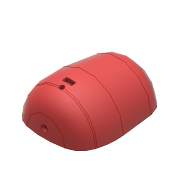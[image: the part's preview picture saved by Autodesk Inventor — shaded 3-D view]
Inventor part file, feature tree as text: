
AUTODESK INVENTOR PART (.ipt)
format: ipt  version: 2017 (Build 210142000, 142)  size: 274,944 bytes
history: native  units: mm
features: sketch x9, extrude x7, fillet x4, projected_geometry x2, revolve x1, chamfer x1, shell x1, hole x1, plane x1
ambient origin geometry x8: Origin, YZ Plane, XZ Plane, XY Plane, X Axis, Y Axis, Z Axis, Center Point
bodies: Solid1 (feature_tree)
feature tree (27):
  revolve  "Revolution1"  [1 undecoded]
  fillet  "Fillet1"  Radius=30.0mm
  chamfer  "Chamfer1"  Distance=10.0mm Angle=45.0deg
  fillet  "Fillet2"  Radius=20.0mm
  fillet  "Fillet3"  Radius=60.0mm
  extrude  "Extrusion1"  Depth=10.0mm
  shell  "Shell1"  Thickness=100.0mm
  extrude  "Extrusion3"  Depth=12.0mm
  extrude  "Extrusion4"  Depth=8.0mm
  hole  "Hole1"  [1 undecoded]
  plane  "Work Plane1"
  extrude  "Extrusion5"  [1 undecoded]
  fillet  "Fillet4"  Radius=6.0mm
  extrude  "Extrusion6"  Depth=10.0mm TaperAngle=0.0deg
  extrude  "Extrusion7"  Depth=2.0mm
  extrude  "Extrusion8"  Depth=10.0mm
  sketch  "Sketch1"  dims[d0=40.0mm d1=80.0mm d2=30.0mm]
  sketch  "Sketch2"  dims[d3=90.0deg]
  sketch  "Sketch4"  dims[d4=20.0mm d5=10.0mm d6=20.0mm d7=45.0deg d8=20.0mm d9=60.0mm]
  sketch  "Sketch5"  dims[d10=10.0mm d11=0.0mm d12=4.0mm d18=100.0mm d20=80.0mm]
  sketch  "Sketch6"  dims[d32=6.0mm d33=12.0mm]
  projected_geometry  "Projected Loop1"
  sketch  "Sketch7"  dims[d34=14.0mm d35=0.0mm d36=8.0mm]
  sketch  "Sketch8"  dims[d37=24.0mm d38=4.0mm d39=0.0mm]
  sketch  "Sketch9"  dims[d40=8.0mm]
  projected_geometry  "Projected Loop2"
  sketch  "Sketch10"  dims[d41=3.5mm d42=6.0mm d43=4.0mm d44=2.0mm d45=90.0deg d46=8.0mm d47=20.594885mm d48=-9.5mm d49=6.0mm d50=4.0mm d51=0.0mm d52=2.0mm d53=20.0mm d54=6.0mm d55=15.0mm d56=33.0mm d57=0.0mm d58=4.0mm d59=1.0mm d60=10.0mm d61=9.0mm d62=32.0mm d63=0.0mm d64=4.0mm d65=8.0mm d66=10.0mm d67=0.0mm]
note: 3 required parameter values undecoded (feature->parameter linkage not recoverable at this tier; creation-order binding heuristic only, values carry confidence <= 0.55)